# Revit family: 1HVAC_Ductwork_Airzone_Supply-Motorized-Curved-Slat-Grille_RIC1
name_source: partatom
category: Air Terminals
revit_build: Autodesk Revit 2016 (Build: 20161004_0715(x64)
units: mm (PartAtom-declared; Revit-internal decimal feet)

## family parameters
Always vertical = Yes
Cut with Voids When Loaded = No
OmniClass Number = 23.75.70.21.27.11
OmniClass Title = Diffusers, Registers, and Grilles
Part Type = Normal
Room Calculation Point = Yes
Round Connector Dimension = Use Diameter
Shared = No
Work Plane-Based = No

## types (1)
- INVALID TYPE - Use Load Family and Type Catalog instead
    Accessories Material = Metal - AIRZONE - Extruded Aluminium - Anodized (Matt Silver Color)
    Actuator Description = MINT - Smart grille actuator - 12V, 40mA, 250mA max, 0.8 Nm
    Ak = 2.53
    Compatible Accesories = Mounting frame. Manual flow regulation. Plenum for grille (PREJ, FR-X2F). Grille deflector
    Description = Curved-slat smart motorized grille
    Disclaimer = All information provided in this model is reviewed before being published. However, Airzone cannot guarantee this model is error-free, therefore users are strongly encouraged to check for technical documentation and updates
    Duct Height = 150 mm
    Duct Width = 300 mm
    Effective Area = 253.00 cm²
    Finish = White (RAL 9010)
    Fixing = Screw (T), mounting frame required
    Grille Material = Metal - AIRZONE - Grille 25 mm - White (RAL 9010)
    Long Description = RIC curved-slat smart grille made of extruded aluminum with 26-mm frame. Made up of two parts: a first row of horizontal slats that can be manually adjusted and a second row of horizontal slats controlled by connecting rod-actuator assembly. It allows you to regulate the air flow to guarantee a perfect air distribution.
    Main Material = Metal - AIRZONE - Extruded Aluminium - White (RAL 9010)
    Manufacturer = AIRZONE
    Max Flow = 1500 m³/h
    Min Flow = 150 m³/h
    Model = INVALID – Type not loaded via type catalog
    Product Code = INVALID – Type not loaded via type catalog
    Product Comments = Refer to technical documentation for further details
    Product Documentation Download URL = http://doc.airzone.es
    Revit Model Version = 1.0
    Type Image Comments = Image available in product documentation download
    URL = www.airzone.es
    c1 = 0.000112
    c2 = -2.091
    c3 = -136.9
    c4 = -15.62
    c5 = 67.31
    c6 = -11.04
    c7 = 0.01545
    c8 = -0.5271

## geometry (parser evidence)
native form markers: Sweep x1
no freeform markers — native parametric forms only
